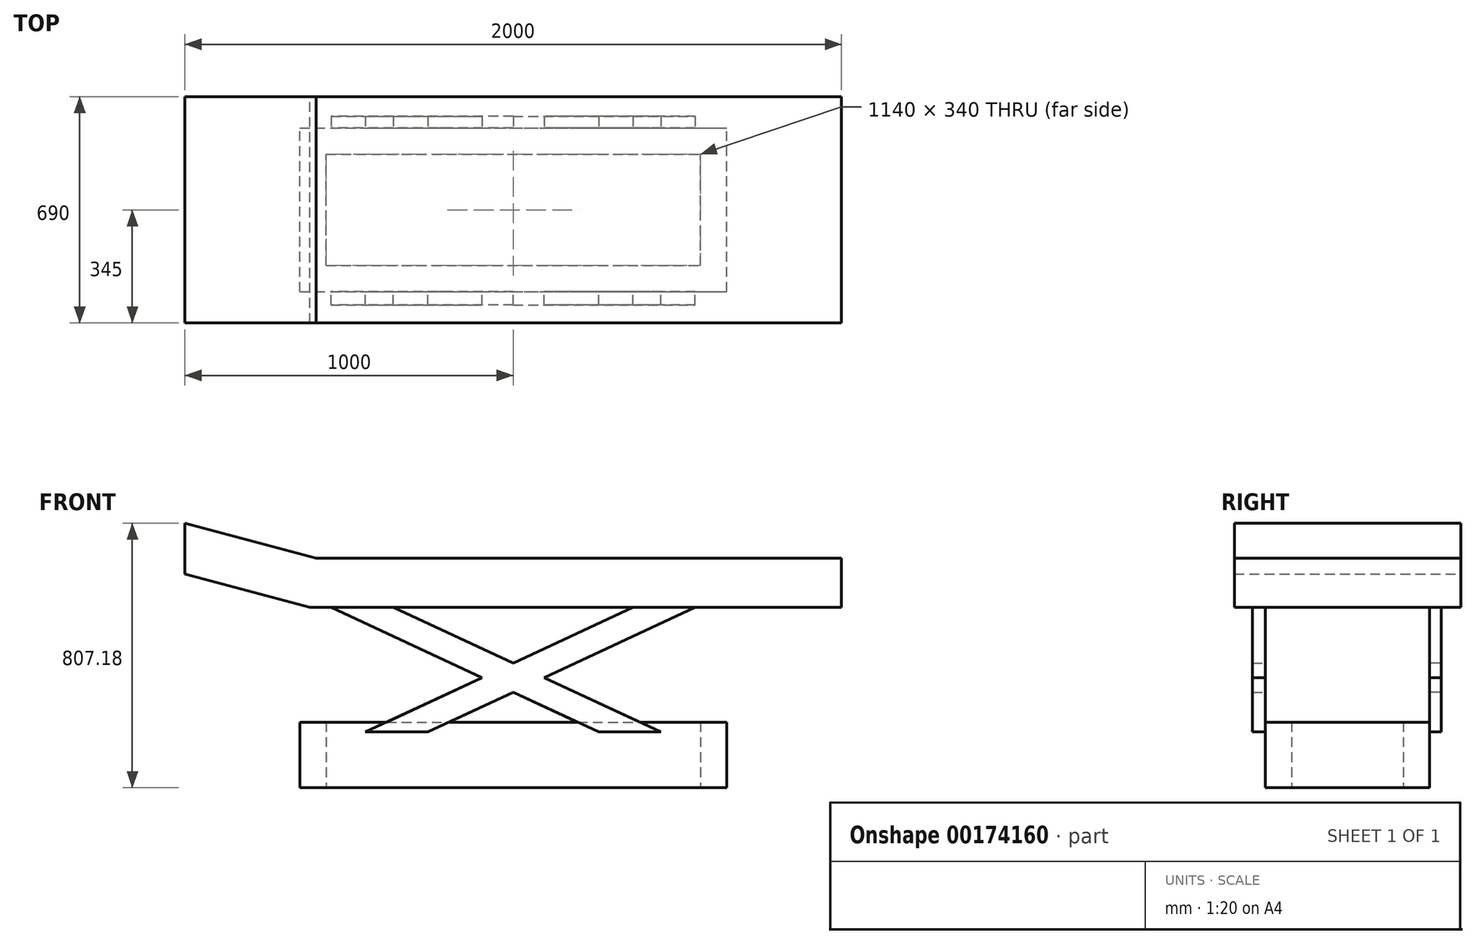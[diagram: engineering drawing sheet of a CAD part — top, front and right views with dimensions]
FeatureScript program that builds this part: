
annotation { "Feature Type Name" : "Feature", "Feature Type Description" : "" }
export const myFeature = defineFeature(function(context is Context, id is Id, definition is map)
    precondition{}
    {
        {
            var Q0;
            Q0=qCreatedBy(makeId("Top.planeOp"),FACE);
            var sketch = newSketch(context, id + "F0", { "sketchPlane" : qUnion([Q0])});
            skLineSegment(sketch, "E0.bottom", {"start": v(-650, -250) * mm, "end": v(650, -250) * mm});
            skLineSegment(sketch, "E0.top", {"start": v(-650, 250) * mm, "end": v(650, 250) * mm});
            skLineSegment(sketch, "E0.left", {"start": v(-650, -250) * mm, "end": v(-650, 250) * mm});
            skLineSegment(sketch, "E0.right", {"start": v(650, -250) * mm, "end": v(650, 250) * mm});
            skLineSegment(sketch, "E1.0", {"start": v(-570, -170) * mm, "end": v(-570, 170) * mm});
            skLineSegment(sketch, "E1.1", {"start": v(-570, -170) * mm, "end": v(570, -170) * mm});
            skLineSegment(sketch, "E1.2", {"start": v(570, -170) * mm, "end": v(570, 170) * mm});
            skLineSegment(sketch, "E1.3", {"start": v(-570, 170) * mm, "end": v(570, 170) * mm});
            skLineSegment(sketch, "E2", {"start": v(-650, -250) * mm, "end": v(650, 250) * mm, "construction": true});
            skLineSegment(sketch, "E3", {"start": v(-650, 250) * mm, "end": v(650, -250) * mm, "construction": true});
            skPoint(sketch, "E4", {"position": v(0, 0) * mm});
            skSolve(sketch);
        }
        {
            var Q0;
            Q0=makeQuery(id+"F0.imprint","IMPRINT",FACE,{"disambiguationData":[TD([[makeQuery(id+"F0.imprint","IMPRINT",EDGE,{"derivedFrom":sQuery(id+"F0.wireOp",EDGE,"E0.bottom")}),1.0]])]});
            extrude(context, id + "F1", {"entities" : qUnion([Q0]), "depth" : 200 * mm});
        }
        {
            var Q0;
            Q0=qCreatedBy(makeId("Front.planeOp"),FACE);
            var sketch = newSketch(context, id + "F2", { "sketchPlane" : qUnion([Q0])});
            skLineSegment(sketch, "E5.bottom", {"start": v(-600, 700) * mm, "end": v(1000, 700) * mm});
            skLineSegment(sketch, "E5.top", {"start": v(-619.75, 550) * mm, "end": v(1000, 550) * mm});
            skLineSegment(sketch, "E5.right", {"start": v(1000, 700) * mm, "end": v(1000, 550) * mm});
            skLineSegment(sketch, "E6", {"start": v(-600, 700) * mm, "end": v(-1000, 807.18) * mm});
            skLineSegment(sketch, "E7", {"start": v(-1000, 807.18) * mm, "end": v(-1000, 651.89) * mm});
            skLineSegment(sketch, "E8", {"start": v(-1000, 651.89) * mm, "end": v(-619.75, 550) * mm});
            skSolve(sketch);
        }
        {
            var Q0;
            Q0=makeQuery(id+"F2.imprint","IMPRINT",FACE,{"disambiguationData":[TD([[makeQuery(id+"F2.imprint","IMPRINT",EDGE,{"derivedFrom":sQuery(id+"F2.wireOp",EDGE,"E5.bottom")}),-1.0]])]});
            extrude(context, id + "F3", {"entities" : qUnion([Q0]), "operationType" : NewBodyOperationType.ADD, "endBound" : BoundingType.SYMMETRIC, "depth" : 690 * mm});
        }
        {
            var Q0;
            Q0=makeQuery(id+"F1.opExtrude","SWEPT_FACE",FACE,{"disambiguationData":[OSD([sQuery(id+"F0.wireOp",EDGE,"E0.bottom")])]});
            var sketch = newSketch(context, id + "F4", { "sketchPlane" : qUnion([Q0])});
            skLineSegment(sketch, "E9", {"start": v(-450, 170) * mm, "end": v(364.91, 550) * mm});
            skLineSegment(sketch, "E10", {"start": v(0, 0) * mm, "end": v(0, 375) * mm, "construction": true});
            skLineSegment(sketch, "E11", {"start": v(364.91, 550) * mm, "end": v(554.2, 550) * mm});
            skLineSegment(sketch, "E12.MirrorCS", {"start": v(-364.91, 550) * mm, "end": v(-554.2, 550) * mm});
            skLineSegment(sketch, "E13", {"start": v(-450, 170) * mm, "end": v(-260.7, 170) * mm});
            skLineSegment(sketch, "E14.MirrorCS", {"start": v(450, 170) * mm, "end": v(260.7, 170) * mm});
            skPoint(sketch, "E15.orphan", {"position": v(0, 287.68) * mm});
            skLineSegment(sketch, "E16", {"start": v(554.2, 550) * mm, "end": v(-260.7, 170) * mm});
            skLineSegment(sketch, "E17.MirrorCS", {"start": v(-554.2, 550) * mm, "end": v(260.7, 170) * mm});
            skLineSegment(sketch, "E18.MirrorCS", {"start": v(450, 170) * mm, "end": v(-364.91, 550) * mm});
            skSolve(sketch);
        }
        {
            var Q0;
            {var subQ5=sQuery(id+"F4.wireOp",EDGE,"E12.MirrorCS");Q0=makeQuery(id+"F4.imprint","IMPRINT",FACE,{"disambiguationData":[TD([[makeQuery(id+"F4.imprint","IMPRINT",EDGE,{"derivedFrom":subQ5}),1.0]])]});}
            var Q1;
            {var subQ0=sQuery(id+"F4.wireOp",EDGE,"E11");Q1=makeQuery(id+"F4.imprint","IMPRINT",FACE,{"disambiguationData":[TD([[makeQuery(id+"F4.imprint","IMPRINT",EDGE,{"derivedFrom":subQ0}),-1.0]])]});}
            var Q2;
            {var subQ0=sQuery(id+"F4.wireOp",EDGE,"8301ae61-d958-4560-9958-04439822b2cd0.MirrorCS");var subQ1=sQuery(id+"F4.wireOp",EDGE,"E9");var subQ2=makeQuery(id+"F4.imprint","INTERSECT",VERTEX,{"derivedFrom":[subQ1,subQ0]});Q2=makeQuery(id+"F4.imprint","IMPRINT",FACE,{"disambiguationData":[TD([[makeQuery(id+"F4.imprint","IMPRINT",EDGE,{"disambiguationData":[TD([[subQ2,-1.0]])],"derivedFrom":subQ1}),-1.0]])]});}
            var Q3;
            {var subQ0=sQuery(id+"F4.wireOp",EDGE,"vlyEdD4a-hHfZ-zw5Z-XqWn-dTF2GS7PxnFV");Q3=makeQuery(id+"F4.imprint","IMPRINT",FACE,{"disambiguationData":[TD([[makeQuery(id+"F4.imprint","IMPRINT",EDGE,{"derivedFrom":subQ0}),1.0]])]});}
            var Q4;
            {var subQ5=sQuery(id+"F4.wireOp",EDGE,"ec0dfd43-2396-4a77-a6fa-ca73278d13110.MirrorCS");Q4=makeQuery(id+"F4.imprint","IMPRINT",FACE,{"disambiguationData":[TD([[makeQuery(id+"F4.imprint","IMPRINT",EDGE,{"derivedFrom":subQ5}),1.0]])]});}
            var Q5;
            {var subQ0=sQuery(id+"F4.wireOp",EDGE,"E18.MirrorCS");var subQ1=sQuery(id+"F4.wireOp",EDGE,"E16");var subQ2=makeQuery(id+"F4.imprint","INTERSECT",VERTEX,{"derivedFrom":[subQ1,subQ0]});Q5=makeQuery(id+"F4.imprint","IMPRINT",FACE,{"disambiguationData":[TD([[makeQuery(id+"F4.imprint","IMPRINT",EDGE,{"disambiguationData":[TD([[subQ2,-1.0]])],"derivedFrom":subQ1}),1.0]])]});}
            var Q6;
            {var subQ0=sQuery(id+"F4.wireOp",EDGE,"E14.MirrorCS");Q6=makeQuery(id+"F4.imprint","IMPRINT",FACE,{"disambiguationData":[TD([[makeQuery(id+"F4.imprint","IMPRINT",EDGE,{"derivedFrom":subQ0}),-1.0]])]});}
            extrude(context, id + "F5", {"entities" : qUnion([Q0, Q1, Q2, Q3, Q4, Q5, Q6]), "operationType" : NewBodyOperationType.ADD, "depth" : 40 * mm});
        }
        {
            var Q0;
            Q0=makeQuery(id+"F1.opExtrude","SWEPT_FACE",FACE,{"disambiguationData":[OSD([sQuery(id+"F0.wireOp",EDGE,"E0.top")])]});
            var sketch = newSketch(context, id + "F6", { "sketchPlane" : qUnion([Q0])});
            skLineSegment(sketch, "E19", {"start": v(-450, 170) * mm, "end": v(364.91, 550) * mm});
            skLineSegment(sketch, "E20", {"start": v(0, -232.38) * mm, "end": v(0, 142.62) * mm, "construction": true});
            skLineSegment(sketch, "E21", {"start": v(364.91, 550) * mm, "end": v(554.2, 550) * mm});
            skLineSegment(sketch, "E22.MirrorCS", {"start": v(-364.91, 550) * mm, "end": v(-554.2, 550) * mm});
            skLineSegment(sketch, "E23", {"start": v(-450, 170) * mm, "end": v(-260.7, 170) * mm});
            skLineSegment(sketch, "E24.MirrorCS", {"start": v(450, 170) * mm, "end": v(260.7, 170) * mm});
            skPoint(sketch, "E25.orphan", {"position": v(-125.96, 55.3) * mm});
            skLineSegment(sketch, "E26", {"start": v(554.2, 550) * mm, "end": v(-260.7, 170) * mm});
            skLineSegment(sketch, "E27.MirrorCS", {"start": v(-554.2, 550) * mm, "end": v(260.7, 170) * mm});
            skLineSegment(sketch, "E28.MirrorCS", {"start": v(450, 170) * mm, "end": v(-364.91, 550) * mm});
            skSolve(sketch);
        }
        {
            var Q0;
            {var subQ5=sQuery(id+"F6.wireOp",EDGE,"E22.MirrorCS");Q0=makeQuery(id+"F6.imprint","IMPRINT",FACE,{"disambiguationData":[TD([[makeQuery(id+"F6.imprint","IMPRINT",EDGE,{"derivedFrom":subQ5}),1.0]])]});}
            var Q1;
            {var subQ0=sQuery(id+"F6.wireOp",EDGE,"E21");Q1=makeQuery(id+"F6.imprint","IMPRINT",FACE,{"disambiguationData":[TD([[makeQuery(id+"F6.imprint","IMPRINT",EDGE,{"derivedFrom":subQ0}),-1.0]])]});}
            var Q2;
            {var subQ0=sQuery(id+"F6.wireOp",EDGE,"E27.MirrorCS");var subQ1=sQuery(id+"F6.wireOp",EDGE,"E19");var subQ2=makeQuery(id+"F6.imprint","INTERSECT",VERTEX,{"derivedFrom":[subQ1,subQ0]});Q2=makeQuery(id+"F6.imprint","IMPRINT",FACE,{"disambiguationData":[TD([[makeQuery(id+"F6.imprint","IMPRINT",EDGE,{"disambiguationData":[TD([[subQ2,-1.0]])],"derivedFrom":subQ1}),-1.0]])]});}
            var Q3;
            {var subQ0=sQuery(id+"F6.wireOp",EDGE,"E27.MirrorCS");var subQ1=sQuery(id+"F6.wireOp",EDGE,"E19");var subQ2=makeQuery(id+"F6.imprint","INTERSECT",VERTEX,{"derivedFrom":[subQ1,subQ0]});Q3=makeQuery(id+"F6.imprint","IMPRINT",FACE,{"disambiguationData":[TD([[makeQuery(id+"F6.imprint","IMPRINT",EDGE,{"disambiguationData":[TD([[subQ2,1.0]])],"derivedFrom":subQ1}),-1.0]])]});}
            var Q4;
            {var subQ0=sQuery(id+"F6.wireOp",EDGE,"E28.MirrorCS");var subQ1=sQuery(id+"F6.wireOp",EDGE,"E26");var subQ2=makeQuery(id+"F6.imprint","INTERSECT",VERTEX,{"derivedFrom":[subQ1,subQ0]});Q4=makeQuery(id+"F6.imprint","IMPRINT",FACE,{"disambiguationData":[TD([[makeQuery(id+"F6.imprint","IMPRINT",EDGE,{"disambiguationData":[TD([[subQ2,-1.0]])],"derivedFrom":subQ1}),1.0]])]});}
            var Q5;
            {var subQ0=sQuery(id+"F6.wireOp",EDGE,"E24.MirrorCS");Q5=makeQuery(id+"F6.imprint","IMPRINT",FACE,{"disambiguationData":[TD([[makeQuery(id+"F6.imprint","IMPRINT",EDGE,{"derivedFrom":subQ0}),-1.0]])]});}
            var Q6;
            {var subQ0=sQuery(id+"F6.wireOp",EDGE,"E23");Q6=makeQuery(id+"F6.imprint","IMPRINT",FACE,{"disambiguationData":[TD([[makeQuery(id+"F6.imprint","IMPRINT",EDGE,{"derivedFrom":subQ0}),1.0]])]});}
            extrude(context, id + "F7", {"entities" : qUnion([Q0, Q1, Q2, Q3, Q4, Q5, Q6]), "operationType" : NewBodyOperationType.ADD, "depth" : 35 * mm});
        }
    });
